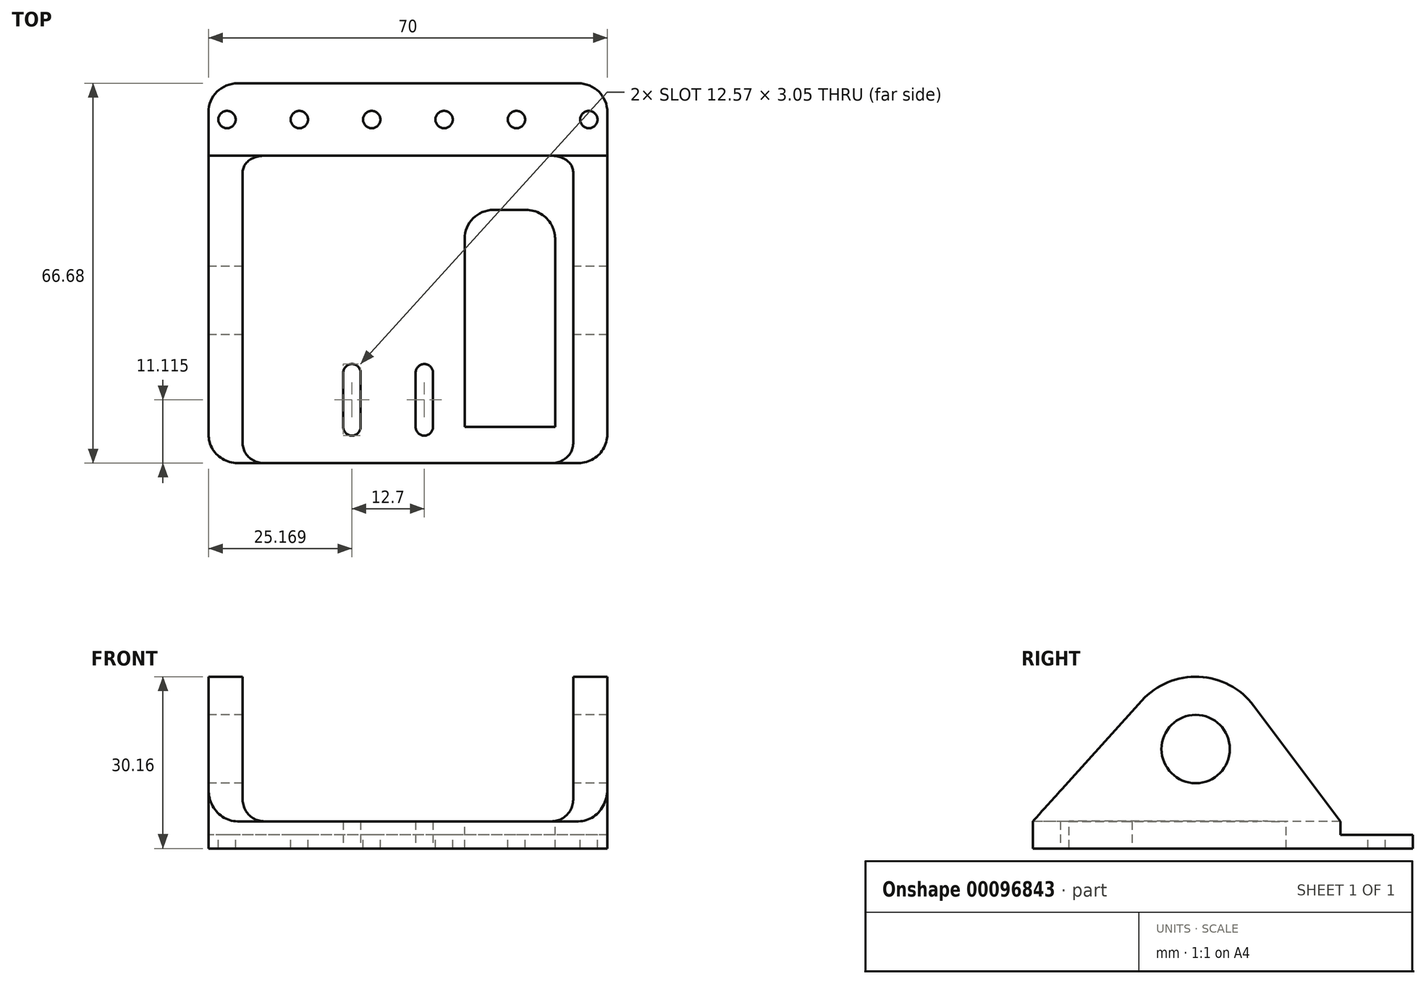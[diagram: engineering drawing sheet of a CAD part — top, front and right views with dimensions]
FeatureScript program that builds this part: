
annotation { "Feature Type Name" : "Feature", "Feature Type Description" : "" }
export const myFeature = defineFeature(function(context is Context, id is Id, definition is map)
    precondition{}
    {
        {
            var Q0;
            Q0=qCreatedBy(makeId("Top.planeOp"),FACE);
            var sketch = newSketch(context, id + "F0", { "sketchPlane" : qUnion([Q0])});
            skLineSegment(sketch, "E0.bottom", {"start": v(35, 33.34) * mm, "end": v(-35, 33.34) * mm});
            skLineSegment(sketch, "E0.top", {"start": v(35, -33.34) * mm, "end": v(-35, -33.34) * mm});
            skLineSegment(sketch, "E0.left", {"start": v(35, 33.34) * mm, "end": v(35, -33.34) * mm});
            skLineSegment(sketch, "E0.right", {"start": v(-35, 33.34) * mm, "end": v(-35, -33.34) * mm});
            skPoint(sketch, "E0.middle", {"position": v(0, 0) * mm});
            skSolve(sketch);
        }
        {
            var Q0;
            Q0 = qSketchRegion(id + "F0", true);
            extrude(context, id + "F1", {"entities" : qUnion([Q0]), "depth" : 4.76 * mm});
        }
        {
            var Q0;
            Q0=makeQuery(id+"F1.opExtrude","SWEPT_FACE",FACE,{"disambiguationData":[OSD([sQuery(id+"F0.wireOp",EDGE,"E0.right")])]});
            var sketch = newSketch(context, id + "F2", { "sketchPlane" : qUnion([Q0])});
            skCircle(sketch, "E1", {"center": v(4.76, 17.46) * mm, "radius": 2 * mm});
            skCircle(sketch, "E2", {"center": v(4.76, 17.46) * mm, "radius": 6 * mm});
            skLineSegment(sketch, "E3", {"start": v(-7.94, 17.46) * mm, "end": v(-7.94, 4.76) * mm});
            skLineSegment(sketch, "E4", {"start": v(-7.94, 4.76) * mm, "end": v(17.46, 4.76) * mm});
            skLineSegment(sketch, "E5", {"start": v(17.46, 4.76) * mm, "end": v(17.46, 17.46) * mm});
            skArc(sketch, "E6", {"start": v(-7.94, 17.46) * mm, "mid": v(-4.22, 8.48) * mm, "end": v(4.76, 4.76) * mm, "construction": true});
            skArc(sketch, "E7", {"start": v(4.76, 4.76) * mm, "mid": v(13.74, 8.48) * mm, "end": v(17.46, 17.46) * mm, "construction": true});
            skArc(sketch, "E8", {"start": v(17.46, 17.46) * mm, "mid": v(4.76, 30.16) * mm, "end": v(-7.94, 17.46) * mm});
            skLineSegment(sketch, "E9", {"start": v(14.19, 25.97) * mm, "end": v(33.34, 4.76) * mm});
            skLineSegment(sketch, "E10", {"start": v(33.34, 4.76) * mm, "end": v(17.46, 4.76) * mm});
            skLineSegment(sketch, "E11", {"start": v(-5.4, 25.08) * mm, "end": v(-20.64, 4.76) * mm});
            skLineSegment(sketch, "E12", {"start": v(-20.64, 4.76) * mm, "end": v(-7.94, 4.76) * mm});
            skSolve(sketch);
        }
        {
            var Q0;
            Q0 = qSketchRegion(id + "F2", true);
            var Q1;
            Q1=makeQuery(id+"F1.opExtrude","SWEPT_FACE",FACE,{"disambiguationData":[OSD([sQuery(id+"F0.wireOp",EDGE,"E0.left")])]});
            extrude(context, id + "F3", {"entities" : qUnion([Q0]), "operationType" : NewBodyOperationType.ADD, "endBound" : BoundingType.UP_TO_SURFACE, "oppositeDirection" : true, "endBoundEntityFace" : qUnion([Q1]), "depth" : 25.4 * mm});
        }
        {
            var Q0;
            Q0=makeQuery(id+"F1.opExtrude","CAP_FACE",FACE,{"disambiguationData":[OSD([sQuery(id+"F0.wireOp",EDGE,"E0.bottom"),sQuery(id+"F0.wireOp",EDGE,"E0.top"),sQuery(id+"F0.wireOp",EDGE,"E0.left"),sQuery(id+"F0.wireOp",EDGE,"E0.right")])],"isStart":false});
            var sketch = newSketch(context, id + "F4", { "sketchPlane" : qUnion([Q0])});
            skLineSegment(sketch, "E13.bottom", {"start": v(-29, 20.64) * mm, "end": v(29, 20.64) * mm});
            skLineSegment(sketch, "E13.top", {"start": v(-29, -33.34) * mm, "end": v(29, -33.34) * mm});
            skLineSegment(sketch, "E13.left", {"start": v(-29, 20.64) * mm, "end": v(-29, -33.34) * mm});
            skLineSegment(sketch, "E13.right", {"start": v(29, 20.64) * mm, "end": v(29, -33.34) * mm});
            skSolve(sketch);
        }
        {
            var Q0;
            Q0 = qSketchRegion(id + "F4", true);
            extrude(context, id + "F5", {"entities" : qUnion([Q0]), "operationType" : NewBodyOperationType.REMOVE, "endBound" : BoundingType.THROUGH_ALL, "depth" : 25.4 * mm});
        }
        {
            var Q0;
            Q0=makeQuery(id+"F5.boolean.opBoolean","MERGE",FACE,{"derivedFrom":[makeQuery(id+"F1.opExtrude","CAP_FACE",FACE,{"disambiguationData":[OSD([sQuery(id+"F0.wireOp",EDGE,"E0.bottom"),sQuery(id+"F0.wireOp",EDGE,"E0.top"),sQuery(id+"F0.wireOp",EDGE,"E0.left"),sQuery(id+"F0.wireOp",EDGE,"E0.right")])],"isStart":false}),makeQuery(id+"F5.opExtrude","CAP_FACE",FACE,{"disambiguationData":[OSD([sQuery(id+"F4.wireOp",EDGE,"E13.bottom"),sQuery(id+"F4.wireOp",EDGE,"E13.top"),sQuery(id+"F4.wireOp",EDGE,"E13.left"),sQuery(id+"F4.wireOp",EDGE,"E13.right")])],"isStart":true})]});
            var sketch = newSketch(context, id + "F6", { "sketchPlane" : qUnion([Q0])});
            skLineSegment(sketch, "E14.bottom", {"start": v(25.83, -26.99) * mm, "end": v(9.95, -26.99) * mm});
            skLineSegment(sketch, "E14.top", {"start": v(25.83, 11.11) * mm, "end": v(9.95, 11.11) * mm});
            skLineSegment(sketch, "E14.left", {"start": v(25.83, -26.99) * mm, "end": v(25.83, 11.11) * mm});
            skLineSegment(sketch, "E14.right", {"start": v(9.95, -26.99) * mm, "end": v(9.95, 11.11) * mm});
            skSolve(sketch);
        }
        {
            var Q0;
            Q0 = qSketchRegion(id + "F6", true);
            extrude(context, id + "F7", {"entities" : qUnion([Q0]), "operationType" : NewBodyOperationType.REMOVE, "endBound" : BoundingType.UP_TO_NEXT, "oppositeDirection" : true, "depth" : 25.4 * mm});
        }
        {
            var Q0;
            Q0=makeQuery(id+"F1.opExtrude","CAP_FACE",FACE,{"disambiguationData":[OSD([sQuery(id+"F0.wireOp",EDGE,"E0.bottom"),sQuery(id+"F0.wireOp",EDGE,"E0.top"),sQuery(id+"F0.wireOp",EDGE,"E0.left"),sQuery(id+"F0.wireOp",EDGE,"E0.right")])],"isStart":true});
            var sketch = newSketch(context, id + "F8", { "sketchPlane" : qUnion([Q0])});
            skLineSegment(sketch, "E15.bottom", {"start": v(-15.8, 33.34) * mm, "end": v(8.84, 33.34) * mm, "construction": true});
            skLineSegment(sketch, "E15.top", {"start": v(-15.8, 4.35) * mm, "end": v(8.84, 4.35) * mm, "construction": true});
            skLineSegment(sketch, "E15.left", {"start": v(-15.8, 33.34) * mm, "end": v(-15.8, 4.35) * mm, "construction": true});
            skLineSegment(sketch, "E15.right", {"start": v(8.84, 33.34) * mm, "end": v(8.84, 4.35) * mm, "construction": true});
            skLineSegment(sketch, "E16", {"start": v(-15.8, 22.23) * mm, "end": v(-9.83, 22.23) * mm, "construction": true});
            skLineSegment(sketch, "E17", {"start": v(2.87, 22.23) * mm, "end": v(8.84, 22.23) * mm, "construction": true});
            skLineSegment(sketch, "E18", {"start": v(-9.83, 22.23) * mm, "end": v(2.87, 22.23) * mm, "construction": true});
            skLineSegment(sketch, "E19.bottom", {"start": v(-11.35, 17.46) * mm, "end": v(-8.3, 17.46) * mm, "construction": true});
            skLineSegment(sketch, "E19.top", {"start": v(-11.35, 26.99) * mm, "end": v(-8.3, 26.99) * mm, "construction": true});
            skLineSegment(sketch, "E19.left", {"start": v(-11.35, 17.46) * mm, "end": v(-11.35, 26.99) * mm});
            skLineSegment(sketch, "E19.right", {"start": v(-8.3, 17.46) * mm, "end": v(-8.3, 26.99) * mm});
            skPoint(sketch, "E19.middle", {"position": v(-9.83, 22.23) * mm});
            skLineSegment(sketch, "E20.bottom", {"start": v(1.34, 17.46) * mm, "end": v(4.4, 17.46) * mm, "construction": true});
            skLineSegment(sketch, "E20.top", {"start": v(1.35, 26.99) * mm, "end": v(4.4, 26.99) * mm, "construction": true});
            skLineSegment(sketch, "E20.left", {"start": v(1.35, 17.46) * mm, "end": v(1.35, 26.99) * mm});
            skLineSegment(sketch, "E20.right", {"start": v(4.4, 17.46) * mm, "end": v(4.4, 26.99) * mm});
            skPoint(sketch, "E20.middle", {"position": v(2.87, 22.23) * mm});
            skArc(sketch, "E21", {"start": v(-11.35, 17.46) * mm, "mid": v(-9.83, 15.94) * mm, "end": v(-8.3, 17.46) * mm});
            skArc(sketch, "E22", {"start": v(1.34, 17.46) * mm, "mid": v(2.87, 15.94) * mm, "end": v(4.4, 17.46) * mm});
            skArc(sketch, "E23", {"start": v(-8.3, 26.99) * mm, "mid": v(-9.83, 28.51) * mm, "end": v(-11.35, 26.99) * mm});
            skArc(sketch, "E24", {"start": v(4.4, 26.99) * mm, "mid": v(2.87, 28.51) * mm, "end": v(1.35, 26.99) * mm});
            skSolve(sketch);
        }
        {
            var Q0;
            Q0=makeQuery(id+"F8.imprint","IMPRINT",FACE,{"disambiguationData":[TD([[makeQuery(id+"F8.imprint","IMPRINT",EDGE,{"derivedFrom":sQuery(id+"F8.wireOp",EDGE,"E20.left")}),-1.0]])]});
            var Q1;
            Q1=makeQuery(id+"F8.imprint","IMPRINT",FACE,{"disambiguationData":[TD([[makeQuery(id+"F8.imprint","IMPRINT",EDGE,{"derivedFrom":sQuery(id+"F8.wireOp",EDGE,"E19.left")}),-1.0]])]});
            extrude(context, id + "F9", {"entities" : qUnion([Q0, Q1]), "operationType" : NewBodyOperationType.REMOVE, "oppositeDirection" : true, "depth" : 25.4 * mm});
        }
        {
            var Q0;
            Q0=makeQuery(id+"FCm2X9aqr08QVEI_1.splitOp","SPLIT",FACE,{"derivedFrom":makeQuery(id+"FB7dtnONbZpMkYq_1.boolean.opBoolean","MERGE",FACE,{"derivedFrom":[makeQuery(id+"FMi2k5xwuVLF3PA_1.boolean.opBoolean","MERGE",FACE,{"derivedFrom":[makeQuery(id+"F5.boolean.opBoolean","MERGE",FACE,{"derivedFrom":[makeQuery(id+"F1.opExtrude","CAP_FACE",FACE,{"disambiguationData":[OSD([sQuery(id+"F0.wireOp",EDGE,"E0.bottom"),sQuery(id+"F0.wireOp",EDGE,"E0.top"),sQuery(id+"F0.wireOp",EDGE,"E0.left"),sQuery(id+"F0.wireOp",EDGE,"E0.right")])],"isStart":false}),makeQuery(id+"F5.opExtrude","CAP_FACE",FACE,{"disambiguationData":[OSD([sQuery(id+"F4.wireOp",EDGE,"E13.bottom"),sQuery(id+"F4.wireOp",EDGE,"E13.top"),sQuery(id+"F4.wireOp",EDGE,"E13.left"),sQuery(id+"F4.wireOp",EDGE,"E13.right")])],"isStart":true})]}),makeQuery(id+"FMi2k5xwuVLF3PA_1.opExtrude","CAP_FACE",FACE,{"disambiguationData":[OSD([sQuery(id+"FTfkWxI29d7fm9c_1.wireOp",EDGE,"U5VrA20J-yWmg-0HZa-dIx8-nOMwWomhaKgW.bottom"),sQuery(id+"FTfkWxI29d7fm9c_1.wireOp",EDGE,"U5VrA20J-yWmg-0HZa-dIx8-nOMwWomhaKgW.top"),sQuery(id+"FTfkWxI29d7fm9c_1.wireOp",EDGE,"U5VrA20J-yWmg-0HZa-dIx8-nOMwWomhaKgW.left"),sQuery(id+"FTfkWxI29d7fm9c_1.wireOp",EDGE,"U5VrA20J-yWmg-0HZa-dIx8-nOMwWomhaKgW.right")])],"isStart":false})]}),makeQuery(id+"FB7dtnONbZpMkYq_1.opExtrude","CAP_FACE",FACE,{"disambiguationData":[OSD([sQuery(id+"FrBCCQyiW6SgCSX_1.wireOp",EDGE,"mjBH3HNc-4qiW-W3lP-ZLe8-cYrq6YZMYFNo"),sQuery(id+"FrBCCQyiW6SgCSX_1.wireOp",EDGE,"n0JCGPxu-1fb2-x5wm-e2xR-ESQF5aKrQkje"),sQuery(id+"FrBCCQyiW6SgCSX_1.wireOp",EDGE,"84PFO3UT-d6lO-mKTi-YjnM-evNH14zkO4eM"),sQuery(id+"FrBCCQyiW6SgCSX_1.wireOp",EDGE,"4GRO5FYG-KxOb-3d1O-tR9n-mdH5JcoPf6cH"),sQuery(id+"FrBCCQyiW6SgCSX_1.wireOp",EDGE,"m2es6RPa-RLP1-cTb9-RGGa-vc4GqjSnDQWD"),sQuery(id+"FrBCCQyiW6SgCSX_1.wireOp",EDGE,"UMJGmRyr-7NXd-P1yE-yibc-kyMIe0C5EN52"),sQuery(id+"FrBCCQyiW6SgCSX_1.wireOp",EDGE,"6lN2ZSX2-TrvR-bXuT-GwBE-q0yeGYqzIHT5")])],"isStart":false})]}),"isFromBackBody":true});
            var sketch = newSketch(context, id + "F10", { "sketchPlane" : qUnion([Q0])});
            skLineSegment(sketch, "E25.bottom", {"start": v(-35, 33.34) * mm, "end": v(35, 33.34) * mm});
            skLineSegment(sketch, "E25.top", {"start": v(-35, 20.64) * mm, "end": v(35, 20.64) * mm});
            skLineSegment(sketch, "E26", {"start": v(35, 20.64) * mm, "end": v(35, 33.34) * mm});
            skLineSegment(sketch, "E27", {"start": v(-35, 20.64) * mm, "end": v(-35, 33.34) * mm});
            skSolve(sketch);
        }
        {
            var Q0;
            Q0 = qSketchRegion(id + "F10", true);
            extrude(context, id + "F11", {"entities" : qUnion([Q0]), "operationType" : NewBodyOperationType.REMOVE, "oppositeDirection" : true, "depth" : 2.38 * mm});
        }
        {
            var Q0;
            Q0=makeQuery(id+"F11.boolean.opBoolean","COPY",FACE,{"derivedFrom":makeQuery(id+"F11.opExtrude","CAP_FACE",FACE,{"disambiguationData":[OSD([sQuery(id+"F10.wireOp",EDGE,"E25.bottom"),sQuery(id+"F10.wireOp",EDGE,"E25.top"),sQuery(id+"F10.wireOp",EDGE,"E25.left"),sQuery(id+"F10.wireOp",EDGE,"E25.right")])],"isStart":false})});
            var sketch = newSketch(context, id + "F12", { "sketchPlane" : qUnion([Q0])});
            skLineSegment(sketch, "E28", {"start": v(-19.05, 26.99) * mm, "end": v(-6.35, 26.99) * mm, "construction": true});
            skLineSegment(sketch, "E29", {"start": v(-6.35, 26.99) * mm, "end": v(6.35, 26.99) * mm, "construction": true});
            skLineSegment(sketch, "E30", {"start": v(6.35, 26.99) * mm, "end": v(19.05, 26.99) * mm, "construction": true});
            skLineSegment(sketch, "E31", {"start": v(-19.05, 26.99) * mm, "end": v(-31.75, 26.99) * mm, "construction": true});
            skLineSegment(sketch, "E32", {"start": v(19.05, 26.99) * mm, "end": v(31.75, 26.99) * mm, "construction": true});
            skLineSegment(sketch, "E33", {"start": v(31.75, 26.99) * mm, "end": v(35, 26.99) * mm, "construction": true});
            skLineSegment(sketch, "E34", {"start": v(-31.75, 26.99) * mm, "end": v(-35, 26.99) * mm, "construction": true});
            skCircle(sketch, "E35", {"center": v(-31.75, 26.99) * mm, "radius": 1.52 * mm});
            skCircle(sketch, "E36", {"center": v(-19.05, 26.99) * mm, "radius": 1.52 * mm});
            skCircle(sketch, "E37", {"center": v(-6.35, 26.99) * mm, "radius": 1.52 * mm});
            skCircle(sketch, "E38", {"center": v(6.35, 26.99) * mm, "radius": 1.52 * mm});
            skCircle(sketch, "E39", {"center": v(19.05, 26.99) * mm, "radius": 1.52 * mm});
            skCircle(sketch, "E40", {"center": v(31.75, 26.99) * mm, "radius": 1.52 * mm});
            skSolve(sketch);
        }
        {
            var Q0;
            Q0 = qSketchRegion(id + "F12", true);
            extrude(context, id + "F13", {"entities" : qUnion([Q0]), "operationType" : NewBodyOperationType.REMOVE, "endBound" : BoundingType.UP_TO_NEXT, "oppositeDirection" : true, "depth" : 25.4 * mm});
        }
        {
            var Q0;
            Q0=makeQuery(id+"F1.opExtrude","SWEPT_EDGE",EDGE,{"disambiguationData":[OSD([sQuery(id+"F0.wireOp",EDGE,"E0.bottom"),sQuery(id+"F0.wireOp",EDGE,"E0.right")])]});
            var Q1;
            Q1=makeQuery(id+"F1.opExtrude","SWEPT_EDGE",EDGE,{"disambiguationData":[OSD([sQuery(id+"F0.wireOp",EDGE,"E0.bottom"),sQuery(id+"F0.wireOp",EDGE,"E0.left")])]});
            fillet(context, id + "F14", {"entities" : qUnion([Q0, Q1]), "radius" : 5.08 * mm, "tangentPropagation" : true, "allowEdgeOverflow" : false});
        }
        {
            var Q0;
            Q0=makeQuery(id+"F5.boolean.opBoolean","COPY",EDGE,{"derivedFrom":makeQuery(id+"F5.opExtrude","CAP_EDGE",EDGE,{"disambiguationData":[OSD([sQuery(id+"F4.wireOp",EDGE,"E13.left")])],"isStart":true})});
            var Q1;
            Q1=makeQuery(id+"F5.boolean.opBoolean","COPY",EDGE,{"derivedFrom":makeQuery(id+"F5.opExtrude","CAP_EDGE",EDGE,{"disambiguationData":[OSD([sQuery(id+"F4.wireOp",EDGE,"E13.right")])],"isStart":true})});
            fillet(context, id + "F15", {"entities" : qUnion([Q0, Q1]), "radius" : 3.8 * mm, "tangentPropagation" : true, "allowEdgeOverflow" : false});
        }
        {
            var Q0;
            Q0=makeQuery(id+"F1.opExtrude","SWEPT_EDGE",EDGE,{"disambiguationData":[OSD([sQuery(id+"F0.wireOp",EDGE,"E0.top"),sQuery(id+"F0.wireOp",EDGE,"E0.left")])]});
            var Q1;
            Q1=makeQuery(id+"F1.opExtrude","SWEPT_EDGE",EDGE,{"disambiguationData":[OSD([sQuery(id+"F0.wireOp",EDGE,"E0.top"),sQuery(id+"F0.wireOp",EDGE,"E0.right")])]});
            fillet(context, id + "F16", {"entities" : qUnion([Q0, Q1]), "radius" : 5.08 * mm, "tangentPropagation" : true, "allowEdgeOverflow" : false});
        }
        {
            var Q0;
            {var subQ0=sQuery(id+"F6.wireOp",EDGE,"E14.left");var subQ1=sQuery(id+"F6.wireOp",EDGE,"E14.top");Q0=makeQuery(id+"F11.boolean.opBoolean","SPLIT",EDGE,{"disambiguationData":[TD([makeQuery(id+"F1.opExtrude","CAP_FACE",FACE,{"disambiguationData":[OSD([sQuery(id+"F0.wireOp",EDGE,"E0.bottom"),sQuery(id+"F0.wireOp",EDGE,"E0.top"),sQuery(id+"F0.wireOp",EDGE,"E0.left"),sQuery(id+"F0.wireOp",EDGE,"E0.right")])],"isStart":true})])],"derivedFrom":makeQuery(id+"F7.boolean.opBoolean","COPY",EDGE,{"derivedFrom":makeQuery(id+"F7.opExtrude","SWEPT_EDGE",EDGE,{"disambiguationData":[OSD([subQ1,subQ0])]})})});}
            var Q1;
            {var subQ0=sQuery(id+"F6.wireOp",EDGE,"E14.right");var subQ1=sQuery(id+"F6.wireOp",EDGE,"E14.top");Q1=makeQuery(id+"F11.boolean.opBoolean","SPLIT",EDGE,{"disambiguationData":[TD([makeQuery(id+"F1.opExtrude","CAP_FACE",FACE,{"disambiguationData":[OSD([sQuery(id+"F0.wireOp",EDGE,"E0.bottom"),sQuery(id+"F0.wireOp",EDGE,"E0.top"),sQuery(id+"F0.wireOp",EDGE,"E0.left"),sQuery(id+"F0.wireOp",EDGE,"E0.right")])],"isStart":true})])],"derivedFrom":makeQuery(id+"F7.boolean.opBoolean","COPY",EDGE,{"derivedFrom":makeQuery(id+"F7.opExtrude","SWEPT_EDGE",EDGE,{"disambiguationData":[OSD([subQ1,subQ0])]})})});}
            fillet(context, id + "F17", {"entities" : qUnion([Q0, Q1]), "radius" : 5.08 * mm, "tangentPropagation" : true, "allowEdgeOverflow" : false});
        }
    });
